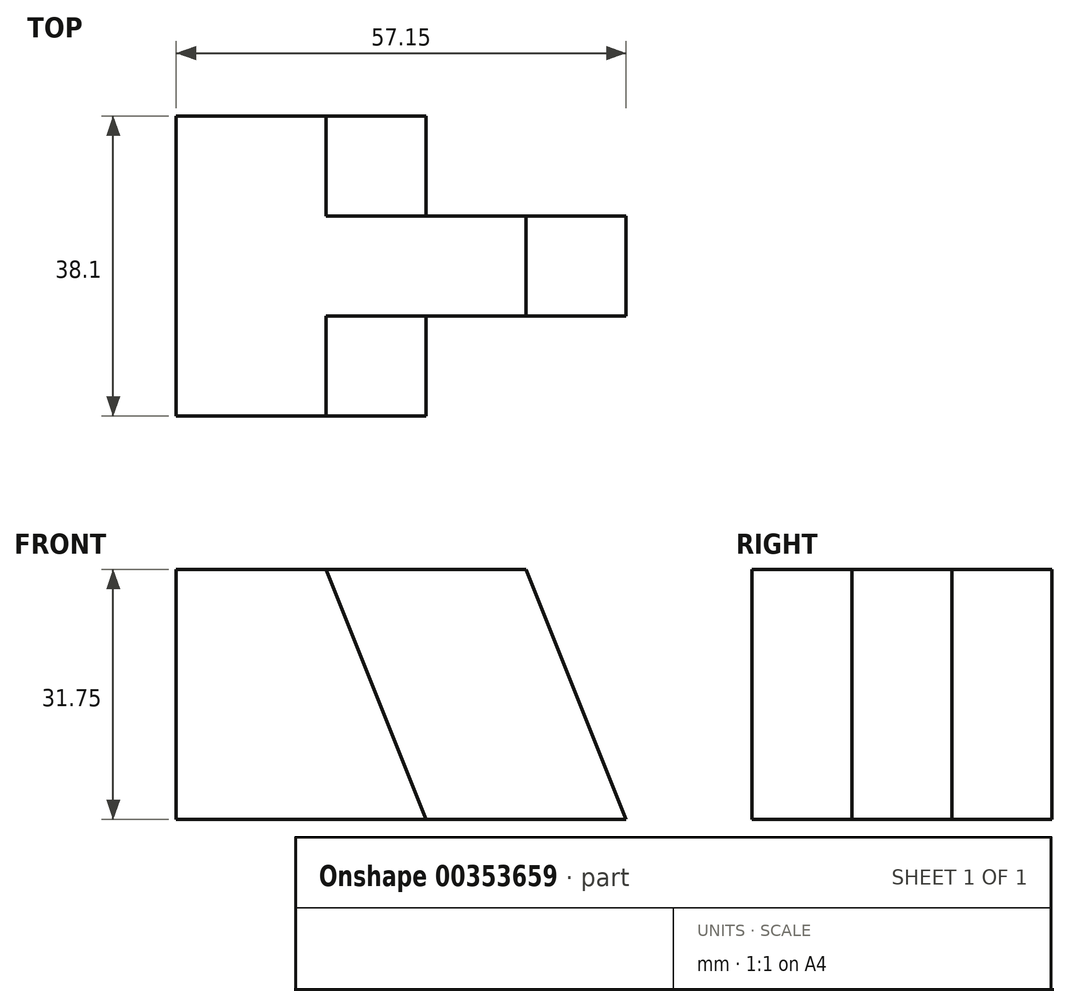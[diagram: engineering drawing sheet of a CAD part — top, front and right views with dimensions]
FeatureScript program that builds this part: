
annotation { "Feature Type Name" : "Feature", "Feature Type Description" : "" }
export const myFeature = defineFeature(function(context is Context, id is Id, definition is map)
    precondition{}
    {
        {
            var Q0;
            Q0=qCreatedBy(makeId("Front.planeOp"),FACE);
            var sketch = newSketch(context, id + "F0", { "sketchPlane" : qUnion([Q0])});
            skLineSegment(sketch, "E0", {"start": v(3.68, 31.75) * mm, "end": v(3.68, 0) * mm});
            skLineSegment(sketch, "E1", {"start": v(3.68, 0) * mm, "end": v(60.83, 0) * mm});
            skLineSegment(sketch, "E2", {"start": v(60.83, 0) * mm, "end": v(60.83, 31.75) * mm});
            skLineSegment(sketch, "E3", {"start": v(60.83, 31.75) * mm, "end": v(3.68, 31.75) * mm});
            skSolve(sketch);
        }
        {
            var Q0;
            Q0=makeQuery(id+"F0.imprint","IMPRINT",FACE,{"disambiguationData":[TD([[makeQuery(id+"F0.imprint","IMPRINT",EDGE,{"derivedFrom":sQuery(id+"F0.wireOp",EDGE,"E0")}),1.0]])]});
            extrude(context, id + "F1", {"entities" : qUnion([Q0]), "depth" : 38.1 * mm});
        }
        {
            var Q0;
            Q0=makeQuery(id+"F1.opExtrude","CAP_FACE",FACE,{"disambiguationData":[OSD([sQuery(id+"F0.wireOp",EDGE,"E0"),sQuery(id+"F0.wireOp",EDGE,"E1"),sQuery(id+"F0.wireOp",EDGE,"E2"),sQuery(id+"F0.wireOp",EDGE,"E3")])],"isStart":false});
            var sketch = newSketch(context, id + "F2", { "sketchPlane" : qUnion([Q0])});
            skLineSegment(sketch, "E4", {"start": v(60.83, 0) * mm, "end": v(48.13, 31.75) * mm});
            skSolve(sketch);
        }
        {
            var Q0;
            {var subQ0=sQuery(id+"F2.wireOp",EDGE,"E4");Q0=makeQuery(id+"F2.imprint","IMPRINT",FACE,{"disambiguationData":[TD([[makeQuery(id+"F2.imprint","IMPRINT",EDGE,{"derivedFrom":subQ0}),-1.0]])]});}
            extrude(context, id + "F3", {"entities" : qUnion([Q0]), "operationType" : NewBodyOperationType.REMOVE, "oppositeDirection" : true, "depth" : 38.1 * mm});
        }
        {
            var Q0;
            Q0=makeQuery(id+"F1.opExtrude","CAP_FACE",FACE,{"disambiguationData":[OSD([sQuery(id+"F0.wireOp",EDGE,"E0"),sQuery(id+"F0.wireOp",EDGE,"E1"),sQuery(id+"F0.wireOp",EDGE,"E2"),sQuery(id+"F0.wireOp",EDGE,"E3")])],"isStart":false});
            var sketch = newSketch(context, id + "F4", { "sketchPlane" : qUnion([Q0])});
            skLineSegment(sketch, "E5", {"start": v(22.73, 31.75) * mm, "end": v(35.43, 0) * mm});
            skSolve(sketch);
        }
        {
            var Q0;
            {var subQ0=sQuery(id+"F4.wireOp",EDGE,"E5");Q0=makeQuery(id+"F4.imprint","IMPRINT",FACE,{"disambiguationData":[TD([[makeQuery(id+"F4.imprint","IMPRINT",EDGE,{"derivedFrom":subQ0}),1.0]])]});}
            extrude(context, id + "F5", {"entities" : qUnion([Q0]), "operationType" : NewBodyOperationType.REMOVE, "oppositeDirection" : true, "depth" : 12.7 * mm});
        }
        {
            var Q0;
            Q0=makeQuery(id+"F1.opExtrude","CAP_FACE",FACE,{"disambiguationData":[OSD([sQuery(id+"F0.wireOp",EDGE,"E0"),sQuery(id+"F0.wireOp",EDGE,"E1"),sQuery(id+"F0.wireOp",EDGE,"E2"),sQuery(id+"F0.wireOp",EDGE,"E3")])],"isStart":true});
            var sketch = newSketch(context, id + "F6", { "sketchPlane" : qUnion([Q0])});
            skLineSegment(sketch, "E6", {"start": v(-22.73, 31.75) * mm, "end": v(-35.43, 0) * mm});
            skSolve(sketch);
        }
        {
            var Q0;
            {var subQ0=sQuery(id+"F6.wireOp",EDGE,"E6");Q0=makeQuery(id+"F6.imprint","IMPRINT",FACE,{"disambiguationData":[TD([[makeQuery(id+"F6.imprint","IMPRINT",EDGE,{"derivedFrom":subQ0}),-1.0]])]});}
            extrude(context, id + "F7", {"entities" : qUnion([Q0]), "operationType" : NewBodyOperationType.REMOVE, "oppositeDirection" : true, "depth" : 12.7 * mm});
        }
    });
